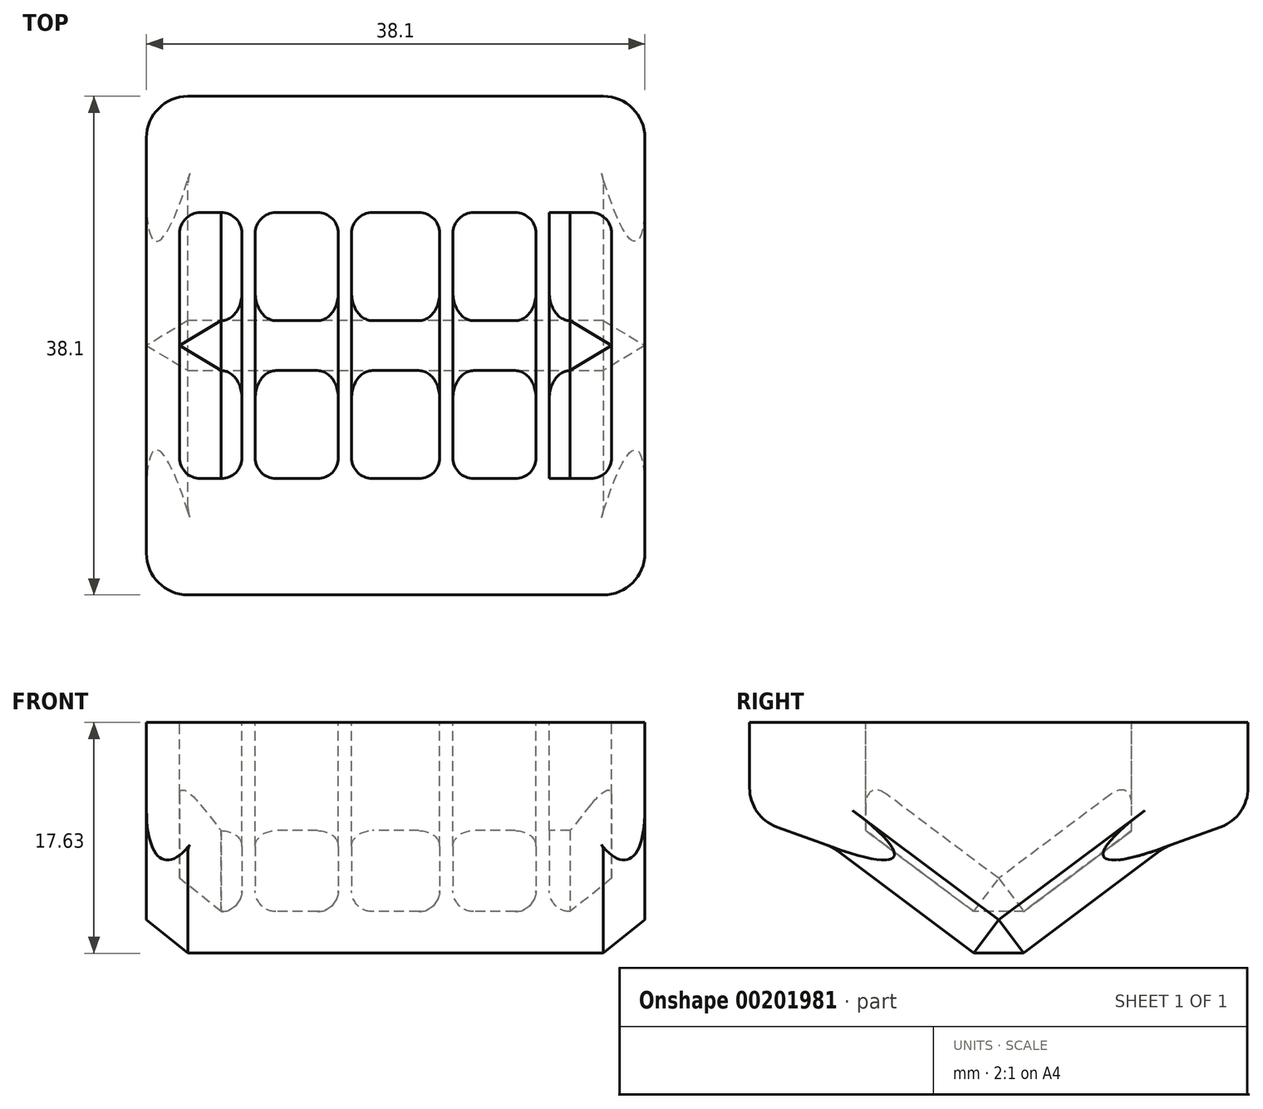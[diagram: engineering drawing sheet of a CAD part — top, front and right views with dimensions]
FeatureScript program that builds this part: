
annotation { "Feature Type Name" : "Feature", "Feature Type Description" : "" }
export const myFeature = defineFeature(function(context is Context, id is Id, definition is map)
    precondition{}
    {
        {
            var Q0;
            Q0=qCreatedBy(makeId("Right.planeOp"),FACE);
            var sketch = newSketch(context, id + "F0", { "sketchPlane" : qUnion([Q0])});
            skLineSegment(sketch, "E0.bottom", {"start": v(12.7, 0) * mm, "end": v(-12.7, 0) * mm});
            skLineSegment(sketch, "E0.top", {"start": v(12.7, 9.53) * mm, "end": v(-12.7, 9.53) * mm});
            skLineSegment(sketch, "E0.left", {"start": v(12.7, 0) * mm, "end": v(12.7, 9.53) * mm});
            skLineSegment(sketch, "E0.right", {"start": v(-12.7, 0) * mm, "end": v(-12.7, 9.53) * mm});
            skPoint(sketch, "E0.middle", {"position": v(0, 4.76) * mm});
            skLineSegment(sketch, "E1", {"start": v(-12.7, 0) * mm, "end": v(0, -9.52) * mm});
            skLineSegment(sketch, "E2", {"start": v(0, -9.52) * mm, "end": v(12.7, 0) * mm});
            skSolve(sketch);
        }
        {
            var Q0;
            Q0 = qSketchRegion(id + "F0", true);
            extrude(context, id + "F1", {"entities" : qUnion([Q0]), "endBound" : BoundingType.SYMMETRIC, "depth" : 38.1 * mm});
        }
        {
            var Q0;
            Q0=makeQuery(id+"F1.opExtrude","SWEPT_FACE",FACE,{"disambiguationData":[OSD([sQuery(id+"F0.wireOp",EDGE,"E0.top")])]});
            shell(context, id + "F2", {"entities" : qUnion([Q0]), "thickness" : 2.54 * mm});
        }
        {
            var Q0;
            Q0=qCreatedBy(makeId("Right.planeOp"),FACE);
            var sketch = newSketch(context, id + "F3", { "sketchPlane" : qUnion([Q0])});
            skLineSegment(sketch, "E3", {"start": v(-12.7, 0) * mm, "end": v(-19.05, 2.31) * mm});
            skLineSegment(sketch, "E4", {"start": v(-19.05, 2.31) * mm, "end": v(-19.05, 9.53) * mm});
            skLineSegment(sketch, "E5", {"start": v(-19.05, 9.53) * mm, "end": v(-12.7, 9.53) * mm});
            skLineSegment(sketch, "E6", {"start": v(-12.7, 9.53) * mm, "end": v(-12.7, 0) * mm});
            skLineSegment(sketch, "E7", {"start": v(0, 0) * mm, "end": v(0, 34.21) * mm, "construction": true});
            skLineSegment(sketch, "E8.MirrorCS", {"start": v(19.05, 2.31) * mm, "end": v(19.05, 9.53) * mm});
            skLineSegment(sketch, "E9.MirrorCS", {"start": v(12.7, 0) * mm, "end": v(19.05, 2.31) * mm});
            skLineSegment(sketch, "E10.MirrorCS", {"start": v(19.05, 9.53) * mm, "end": v(12.7, 9.53) * mm});
            skLineSegment(sketch, "E11.MirrorCS", {"start": v(12.7, 9.53) * mm, "end": v(12.7, 0) * mm});
            skSolve(sketch);
        }
        {
            var Q0;
            Q0 = qSketchRegion(id + "F3", true);
            extrude(context, id + "F4", {"entities" : qUnion([Q0]), "operationType" : NewBodyOperationType.ADD, "endBound" : BoundingType.SYMMETRIC, "depth" : 38.1 * mm});
        }
        {
            var Q0;
            Q0=makeQuery(id+"F4.boolean.opBoolean","MERGE",FACE,{"derivedFrom":[makeQuery(id+"F1.opExtrude","SWEPT_FACE",FACE,{"disambiguationData":[OSD([sQuery(id+"F0.wireOp",EDGE,"E0.top")])]}),makeQuery(id+"F4.opExtrude","SWEPT_FACE",FACE,{"disambiguationData":[OSD([sQuery(id+"F3.wireOp",EDGE,"E5")])]}),makeQuery(id+"F4.opExtrude","SWEPT_FACE",FACE,{"disambiguationData":[OSD([sQuery(id+"F3.wireOp",EDGE,"E10.MirrorCS")])]})]});
            var sketch = newSketch(context, id + "F5", { "sketchPlane" : qUnion([Q0])});
            skLineSegment(sketch, "E12.bottom", {"start": v(-11.75, 10.16) * mm, "end": v(-10.73, 10.16) * mm});
            skLineSegment(sketch, "E12.top", {"start": v(-11.75, -10.16) * mm, "end": v(-10.73, -10.16) * mm});
            skLineSegment(sketch, "E12.left", {"start": v(-11.75, 10.16) * mm, "end": v(-11.75, -10.16) * mm});
            skLineSegment(sketch, "E12.right", {"start": v(-10.73, 10.16) * mm, "end": v(-10.73, -10.16) * mm});
            skPoint(sketch, "E12.middle", {"position": v(-11.24, 0) * mm});
            skLineSegment(sketch, "E13.bottom", {"start": v(-4.38, 10.16) * mm, "end": v(-3.37, 10.16) * mm});
            skLineSegment(sketch, "E13.top", {"start": v(-4.38, -10.16) * mm, "end": v(-3.37, -10.16) * mm});
            skLineSegment(sketch, "E13.left", {"start": v(-4.38, 10.16) * mm, "end": v(-4.38, -10.16) * mm});
            skLineSegment(sketch, "E13.right", {"start": v(-3.37, 10.16) * mm, "end": v(-3.37, -10.16) * mm});
            skPoint(sketch, "E13.middle", {"position": v(-3.87, 0) * mm});
            skLineSegment(sketch, "E14", {"start": v(0, 0) * mm, "end": v(0, 12.03) * mm, "construction": true});
            skPoint(sketch, "E14.endSnap0", {"position": v(0, 10.16) * mm});
            skPoint(sketch, "E15.MirrorP", {"position": v(3.87, 0) * mm});
            skPoint(sketch, "E16.MirrorP", {"position": v(11.24, 0) * mm});
            skLineSegment(sketch, "E17.MirrorCS", {"start": v(4.38, 10.16) * mm, "end": v(4.38, -10.16) * mm});
            skLineSegment(sketch, "E18.MirrorCS", {"start": v(4.38, -10.16) * mm, "end": v(3.37, -10.16) * mm});
            skLineSegment(sketch, "E19.MirrorCS", {"start": v(11.75, -10.16) * mm, "end": v(10.73, -10.16) * mm});
            skLineSegment(sketch, "E20.MirrorCS", {"start": v(10.73, 10.16) * mm, "end": v(10.73, -10.16) * mm});
            skLineSegment(sketch, "E21.MirrorCS", {"start": v(4.38, 10.16) * mm, "end": v(3.37, 10.16) * mm});
            skLineSegment(sketch, "E22.MirrorCS", {"start": v(11.75, 10.16) * mm, "end": v(10.73, 10.16) * mm});
            skLineSegment(sketch, "E23.MirrorCS", {"start": v(3.37, 10.16) * mm, "end": v(3.37, -10.16) * mm});
            skLineSegment(sketch, "E24.MirrorCS", {"start": v(11.75, 10.16) * mm, "end": v(11.75, -10.16) * mm});
            skSolve(sketch);
        }
        {
            var Q0;
            Q0 = qSketchRegion(id + "F5", true);
            extrude(context, id + "F6", {"entities" : qUnion([Q0]), "operationType" : NewBodyOperationType.ADD, "endBound" : BoundingType.UP_TO_NEXT, "oppositeDirection" : true, "depth" : 25.4 * mm});
        }
        {
            var Q0;
            Q0=makeQuery(id+"F1.opExtrude","CAP_EDGE",EDGE,{"disambiguationData":[OSD([sQuery(id+"F0.wireOp",EDGE,"E1")])],"isStart":false});
            var Q1;
            Q1=makeQuery(id+"F1.opExtrude","CAP_EDGE",EDGE,{"disambiguationData":[OSD([sQuery(id+"F0.wireOp",EDGE,"E2")])],"isStart":false});
            var Q2;
            {var subQ0=sQuery(id+"F0.wireOp",EDGE,"E1");Q2=makeQuery(id+"F2.opShell","OFFSET_EDGE",EDGE,{"disambiguationData":[OSD([subQ0]),TDD([makeQuery(id+"F1.opExtrude","CAP_EDGE",EDGE,{"disambiguationData":[OSD([subQ0])],"isStart":false})])]});}
            var Q3;
            {var subQ0=sQuery(id+"F0.wireOp",EDGE,"E2");Q3=makeQuery(id+"F2.opShell","OFFSET_EDGE",EDGE,{"disambiguationData":[OSD([subQ0]),TDD([makeQuery(id+"F1.opExtrude","CAP_EDGE",EDGE,{"disambiguationData":[OSD([subQ0])],"isStart":false})])]});}
            var Q4;
            Q4=makeQuery(id+"F1.opExtrude","CAP_EDGE",EDGE,{"disambiguationData":[OSD([sQuery(id+"F0.wireOp",EDGE,"E1")])],"isStart":true});
            var Q5;
            Q5=makeQuery(id+"F1.opExtrude","CAP_EDGE",EDGE,{"disambiguationData":[OSD([sQuery(id+"F0.wireOp",EDGE,"E2")])],"isStart":true});
            var Q6;
            {var subQ0=sQuery(id+"F0.wireOp",EDGE,"E1");Q6=makeQuery(id+"F2.opShell","OFFSET_EDGE",EDGE,{"disambiguationData":[OSD([subQ0]),TDD([makeQuery(id+"F1.opExtrude","CAP_EDGE",EDGE,{"disambiguationData":[OSD([subQ0])],"isStart":true})])]});}
            var Q7;
            {var subQ0=sQuery(id+"F0.wireOp",EDGE,"E2");Q7=makeQuery(id+"F2.opShell","OFFSET_EDGE",EDGE,{"disambiguationData":[OSD([subQ0]),TDD([makeQuery(id+"F1.opExtrude","CAP_EDGE",EDGE,{"disambiguationData":[OSD([subQ0])],"isStart":true})])]});}
            var Q8;
            Q8=makeQuery(id+"F2.opShell","OFFSET_EDGE",EDGE,{"disambiguationData":[OSD([sQuery(id+"F0.wireOp",EDGE,"E1"),sQuery(id+"F0.wireOp",EDGE,"E2")])]});
            var Q9;
            Q9=makeQuery(id+"F1.opExtrude","SWEPT_EDGE",EDGE,{"disambiguationData":[OSD([sQuery(id+"F0.wireOp",EDGE,"E1"),sQuery(id+"F0.wireOp",EDGE,"E2")])]});
            chamfer(context, id + "F7", {"entities" : qUnion([Q0, Q1, Q2, Q3, Q4, Q5, Q6, Q7, Q8, Q9]), "width" : 3.17 * mm, "tangentPropagation" : true});
        }
        {
            var Q0;
            Q0=makeQuery(id+"F4.opExtrude","CAP_EDGE",EDGE,{"disambiguationData":[OSD([sQuery(id+"F3.wireOp",EDGE,"E3")])],"isStart":true});
            var Q1;
            Q1=makeQuery(id+"F4.opExtrude","CAP_EDGE",EDGE,{"disambiguationData":[OSD([sQuery(id+"F3.wireOp",EDGE,"E9.MirrorCS")])],"isStart":true});
            var Q2;
            Q2=makeQuery(id+"F4.opExtrude","CAP_EDGE",EDGE,{"disambiguationData":[OSD([sQuery(id+"F3.wireOp",EDGE,"E8.MirrorCS")])],"isStart":true});
            var Q3;
            Q3=makeQuery(id+"F4.opExtrude","CAP_EDGE",EDGE,{"disambiguationData":[OSD([sQuery(id+"F3.wireOp",EDGE,"E4")])],"isStart":true});
            var Q4;
            Q4=makeQuery(id+"F4.opExtrude","CAP_EDGE",EDGE,{"disambiguationData":[OSD([sQuery(id+"F3.wireOp",EDGE,"E3")])],"isStart":false});
            var Q5;
            Q5=makeQuery(id+"F4.opExtrude","CAP_EDGE",EDGE,{"disambiguationData":[OSD([sQuery(id+"F3.wireOp",EDGE,"E9.MirrorCS")])],"isStart":false});
            var Q6;
            Q6=makeQuery(id+"F4.opExtrude","CAP_EDGE",EDGE,{"disambiguationData":[OSD([sQuery(id+"F3.wireOp",EDGE,"E4")])],"isStart":false});
            var Q7;
            Q7=makeQuery(id+"F4.boolean.opBoolean","MERGE",EDGE,{"derivedFrom":[makeQuery(id+"F1.opExtrude","SWEPT_EDGE",EDGE,{"disambiguationData":[OSD([sQuery(id+"F0.wireOp",EDGE,"E0.bottom"),sQuery(id+"F0.wireOp",EDGE,"E0.right"),sQuery(id+"F0.wireOp",EDGE,"E1")])]}),makeQuery(id+"F4.opExtrude","SWEPT_EDGE",EDGE,{"disambiguationData":[OSD([sQuery(id+"F3.wireOp",EDGE,"E3"),sQuery(id+"F3.wireOp",EDGE,"E6")])]})]});
            var Q8;
            Q8=makeQuery(id+"F4.opExtrude","SWEPT_EDGE",EDGE,{"disambiguationData":[OSD([sQuery(id+"F3.wireOp",EDGE,"E3"),sQuery(id+"F3.wireOp",EDGE,"E4")])]});
            var Q9;
            Q9=makeQuery(id+"F4.boolean.opBoolean","MERGE",EDGE,{"derivedFrom":[makeQuery(id+"F1.opExtrude","SWEPT_EDGE",EDGE,{"disambiguationData":[OSD([sQuery(id+"F0.wireOp",EDGE,"E0.bottom"),sQuery(id+"F0.wireOp",EDGE,"E0.left"),sQuery(id+"F0.wireOp",EDGE,"E2")])]}),makeQuery(id+"F4.opExtrude","SWEPT_EDGE",EDGE,{"disambiguationData":[OSD([sQuery(id+"F3.wireOp",EDGE,"E9.MirrorCS"),sQuery(id+"F3.wireOp",EDGE,"E11.MirrorCS")])]})]});
            var Q10;
            Q10=makeQuery(id+"F4.opExtrude","SWEPT_EDGE",EDGE,{"disambiguationData":[OSD([sQuery(id+"F3.wireOp",EDGE,"E8.MirrorCS"),sQuery(id+"F3.wireOp",EDGE,"E9.MirrorCS")])]});
            var Q11;
            Q11=makeQuery(id+"F4.opExtrude","CAP_EDGE",EDGE,{"disambiguationData":[OSD([sQuery(id+"F3.wireOp",EDGE,"E8.MirrorCS")])],"isStart":false});
            fillet(context, id + "F8", {"entities" : qUnion([Q0, Q1, Q2, Q3, Q4, Q5, Q6, Q7, Q8, Q9, Q10, Q11]), "radius" : 3.17 * mm, "tangentPropagation" : true, "allowEdgeOverflow" : false});
        }
        {
            var Q0;
            {var subQ0=sQuery(id+"F0.wireOp",EDGE,"E0.right");Q0=makeQuery(id+"F2.opShell","OFFSET_EDGE",EDGE,{"disambiguationData":[OSD([subQ0]),TDD([makeQuery(id+"F1.opExtrude","CAP_EDGE",EDGE,{"disambiguationData":[OSD([subQ0])],"isStart":false})])]});}
            var Q1;
            Q1=makeQuery(id+"F6.opExtrude","SWEPT_EDGE",EDGE,{"disambiguationData":[OSD([sQuery(id+"F0.wireOp",EDGE,"E0.top"),sQuery(id+"F0.wireOp",EDGE,"E0.right"),sQuery(id+"F5.wireOp",EDGE,"E19.MirrorCS"),sQuery(id+"F5.wireOp",EDGE,"E20.MirrorCS")])]});
            var Q2;
            Q2=makeQuery(id+"F6.opExtrude","SWEPT_EDGE",EDGE,{"disambiguationData":[OSD([sQuery(id+"F0.wireOp",EDGE,"E0.top"),sQuery(id+"F0.wireOp",EDGE,"E0.right"),sQuery(id+"F5.wireOp",EDGE,"E18.MirrorCS"),sQuery(id+"F5.wireOp",EDGE,"E23.MirrorCS")])]});
            var Q3;
            Q3=makeQuery(id+"F6.opExtrude","SWEPT_EDGE",EDGE,{"disambiguationData":[OSD([sQuery(id+"F0.wireOp",EDGE,"E0.top"),sQuery(id+"F0.wireOp",EDGE,"E0.right"),sQuery(id+"F5.wireOp",EDGE,"E13.top"),sQuery(id+"F5.wireOp",EDGE,"E13.left")])]});
            var Q4;
            Q4=makeQuery(id+"F6.opExtrude","SWEPT_EDGE",EDGE,{"disambiguationData":[OSD([sQuery(id+"F0.wireOp",EDGE,"E0.top"),sQuery(id+"F0.wireOp",EDGE,"E0.right"),sQuery(id+"F5.wireOp",EDGE,"E12.top"),sQuery(id+"F5.wireOp",EDGE,"E12.left")])]});
            var Q5;
            Q5=makeQuery(id+"F6.opExtrude","SWEPT_EDGE",EDGE,{"disambiguationData":[OSD([sQuery(id+"F0.wireOp",EDGE,"E0.top"),sQuery(id+"F0.wireOp",EDGE,"E0.right"),sQuery(id+"F5.wireOp",EDGE,"E19.MirrorCS"),sQuery(id+"F5.wireOp",EDGE,"E24.MirrorCS")])]});
            var Q6;
            Q6=makeQuery(id+"F6.opExtrude","SWEPT_EDGE",EDGE,{"disambiguationData":[OSD([sQuery(id+"F0.wireOp",EDGE,"E0.top"),sQuery(id+"F0.wireOp",EDGE,"E0.right"),sQuery(id+"F5.wireOp",EDGE,"E17.MirrorCS"),sQuery(id+"F5.wireOp",EDGE,"E18.MirrorCS")])]});
            var Q7;
            Q7=makeQuery(id+"F6.opExtrude","SWEPT_EDGE",EDGE,{"disambiguationData":[OSD([sQuery(id+"F0.wireOp",EDGE,"E0.top"),sQuery(id+"F0.wireOp",EDGE,"E0.right"),sQuery(id+"F5.wireOp",EDGE,"E13.top"),sQuery(id+"F5.wireOp",EDGE,"E13.right")])]});
            var Q8;
            Q8=makeQuery(id+"F6.opExtrude","SWEPT_EDGE",EDGE,{"disambiguationData":[OSD([sQuery(id+"F0.wireOp",EDGE,"E0.top"),sQuery(id+"F0.wireOp",EDGE,"E0.right"),sQuery(id+"F5.wireOp",EDGE,"E12.top"),sQuery(id+"F5.wireOp",EDGE,"E12.right")])]});
            var Q9;
            {var subQ0=sQuery(id+"F0.wireOp",EDGE,"E0.right");Q9=makeQuery(id+"F2.opShell","OFFSET_EDGE",EDGE,{"disambiguationData":[OSD([subQ0]),TDD([makeQuery(id+"F1.opExtrude","CAP_EDGE",EDGE,{"disambiguationData":[OSD([subQ0])],"isStart":true})])]});}
            var Q10;
            Q10=makeQuery(id+"F6.opExtrude","SWEPT_EDGE",EDGE,{"disambiguationData":[OSD([sQuery(id+"F0.wireOp",EDGE,"E0.top"),sQuery(id+"F0.wireOp",EDGE,"E0.left"),sQuery(id+"F5.wireOp",EDGE,"E22.MirrorCS"),sQuery(id+"F5.wireOp",EDGE,"E24.MirrorCS")])]});
            var Q11;
            Q11=makeQuery(id+"F6.opExtrude","SWEPT_EDGE",EDGE,{"disambiguationData":[OSD([sQuery(id+"F0.wireOp",EDGE,"E0.top"),sQuery(id+"F0.wireOp",EDGE,"E0.left"),sQuery(id+"F5.wireOp",EDGE,"E17.MirrorCS"),sQuery(id+"F5.wireOp",EDGE,"E21.MirrorCS")])]});
            var Q12;
            Q12=makeQuery(id+"F6.opExtrude","SWEPT_EDGE",EDGE,{"disambiguationData":[OSD([sQuery(id+"F0.wireOp",EDGE,"E0.top"),sQuery(id+"F0.wireOp",EDGE,"E0.left"),sQuery(id+"F5.wireOp",EDGE,"E13.bottom"),sQuery(id+"F5.wireOp",EDGE,"E13.right")])]});
            var Q13;
            Q13=makeQuery(id+"F6.opExtrude","SWEPT_EDGE",EDGE,{"disambiguationData":[OSD([sQuery(id+"F0.wireOp",EDGE,"E0.top"),sQuery(id+"F0.wireOp",EDGE,"E0.left"),sQuery(id+"F5.wireOp",EDGE,"E12.bottom"),sQuery(id+"F5.wireOp",EDGE,"E12.right")])]});
            var Q14;
            {var subQ0=sQuery(id+"F0.wireOp",EDGE,"E0.left");Q14=makeQuery(id+"F2.opShell","OFFSET_EDGE",EDGE,{"disambiguationData":[OSD([subQ0]),TDD([makeQuery(id+"F1.opExtrude","CAP_EDGE",EDGE,{"disambiguationData":[OSD([subQ0])],"isStart":true})])]});}
            var Q15;
            {var subQ0=sQuery(id+"F0.wireOp",EDGE,"E0.left");Q15=makeQuery(id+"F2.opShell","OFFSET_EDGE",EDGE,{"disambiguationData":[OSD([subQ0]),TDD([makeQuery(id+"F1.opExtrude","CAP_EDGE",EDGE,{"disambiguationData":[OSD([subQ0])],"isStart":false})])]});}
            var Q16;
            Q16=makeQuery(id+"F6.opExtrude","SWEPT_EDGE",EDGE,{"disambiguationData":[OSD([sQuery(id+"F0.wireOp",EDGE,"E0.top"),sQuery(id+"F0.wireOp",EDGE,"E0.left"),sQuery(id+"F5.wireOp",EDGE,"E20.MirrorCS"),sQuery(id+"F5.wireOp",EDGE,"E22.MirrorCS")])]});
            var Q17;
            Q17=makeQuery(id+"F6.opExtrude","SWEPT_EDGE",EDGE,{"disambiguationData":[OSD([sQuery(id+"F0.wireOp",EDGE,"E0.top"),sQuery(id+"F0.wireOp",EDGE,"E0.left"),sQuery(id+"F5.wireOp",EDGE,"E21.MirrorCS"),sQuery(id+"F5.wireOp",EDGE,"E23.MirrorCS")])]});
            var Q18;
            Q18=makeQuery(id+"F6.opExtrude","SWEPT_EDGE",EDGE,{"disambiguationData":[OSD([sQuery(id+"F0.wireOp",EDGE,"E0.top"),sQuery(id+"F0.wireOp",EDGE,"E0.left"),sQuery(id+"F5.wireOp",EDGE,"E13.bottom"),sQuery(id+"F5.wireOp",EDGE,"E13.left")])]});
            var Q19;
            Q19=makeQuery(id+"F6.opExtrude","SWEPT_EDGE",EDGE,{"disambiguationData":[OSD([sQuery(id+"F0.wireOp",EDGE,"E0.top"),sQuery(id+"F0.wireOp",EDGE,"E0.left"),sQuery(id+"F5.wireOp",EDGE,"E12.bottom"),sQuery(id+"F5.wireOp",EDGE,"E12.left")])]});
            var Q20;
            {var subQ0=makeQuery(id+"F6.opExtrude","SWEPT_FACE",FACE,{"disambiguationData":[OSD([sQuery(id+"F5.wireOp",EDGE,"E13.right")])]});var subQ1=sQuery(id+"F0.wireOp",EDGE,"E1");var subQ2=sQuery(id+"F0.wireOp",EDGE,"E2");Q20=makeQuery(id+"F7.opChamfer","BLEND_EDGE",EDGE,{"blendedFrom":[makeQuery(id+"F6.boolean.opBoolean","SPLIT",EDGE,{"disambiguationData":[TD([subQ0])],"derivedFrom":makeQuery(id+"F2.opShell","OFFSET_EDGE",EDGE,{"disambiguationData":[OSD([subQ1,subQ2])]})}),subQ0],"blendedInto":[subQ0]});}
            var Q21;
            {var subQ0=makeQuery(id+"F6.opExtrude","SWEPT_FACE",FACE,{"disambiguationData":[OSD([sQuery(id+"F5.wireOp",EDGE,"E24.MirrorCS")])]});var subQ1=sQuery(id+"F0.wireOp",EDGE,"E2");var subQ2=sQuery(id+"F0.wireOp",EDGE,"E1");Q21=makeQuery(id+"F7.opChamfer","BLEND_EDGE",EDGE,{"blendedFrom":[makeQuery(id+"F6.boolean.opBoolean","SPLIT",EDGE,{"disambiguationData":[TD([subQ0])],"derivedFrom":makeQuery(id+"F2.opShell","OFFSET_EDGE",EDGE,{"disambiguationData":[OSD([subQ2,subQ1])]})}),subQ0],"blendedInto":[subQ0]});}
            var Q22;
            {var subQ0=makeQuery(id+"F6.opExtrude","SWEPT_FACE",FACE,{"disambiguationData":[OSD([sQuery(id+"F5.wireOp",EDGE,"E17.MirrorCS")])]});var subQ1=sQuery(id+"F0.wireOp",EDGE,"E1");var subQ2=sQuery(id+"F0.wireOp",EDGE,"E2");Q22=makeQuery(id+"F7.opChamfer","BLEND_EDGE",EDGE,{"blendedFrom":[makeQuery(id+"F6.boolean.opBoolean","SPLIT",EDGE,{"disambiguationData":[TD([subQ0])],"derivedFrom":makeQuery(id+"F2.opShell","OFFSET_EDGE",EDGE,{"disambiguationData":[OSD([subQ1,subQ2])]})}),subQ0],"blendedInto":[subQ0]});}
            var Q23;
            {var subQ0=makeQuery(id+"F6.opExtrude","SWEPT_FACE",FACE,{"disambiguationData":[OSD([sQuery(id+"F5.wireOp",EDGE,"E12.right")])]});var subQ1=sQuery(id+"F0.wireOp",EDGE,"E1");var subQ2=sQuery(id+"F0.wireOp",EDGE,"E2");Q23=makeQuery(id+"F7.opChamfer","BLEND_EDGE",EDGE,{"blendedFrom":[makeQuery(id+"F6.boolean.opBoolean","SPLIT",EDGE,{"disambiguationData":[TD([subQ0])],"derivedFrom":makeQuery(id+"F2.opShell","OFFSET_EDGE",EDGE,{"disambiguationData":[OSD([subQ1,subQ2])]})}),subQ0],"blendedInto":[subQ0]});}
            var Q24;
            {var subQ0=makeQuery(id+"F6.opExtrude","SWEPT_FACE",FACE,{"disambiguationData":[OSD([sQuery(id+"F5.wireOp",EDGE,"E20.MirrorCS")])]});var subQ1=sQuery(id+"F0.wireOp",EDGE,"E1");var subQ2=sQuery(id+"F0.wireOp",EDGE,"E2");Q24=makeQuery(id+"F7.opChamfer","BLEND_EDGE",EDGE,{"blendedFrom":[makeQuery(id+"F6.boolean.opBoolean","SPLIT",EDGE,{"disambiguationData":[TD([makeQuery(id+"F6.opExtrude","SWEPT_FACE",FACE,{"disambiguationData":[OSD([sQuery(id+"F5.wireOp",EDGE,"E17.MirrorCS")])]})])],"derivedFrom":makeQuery(id+"F2.opShell","OFFSET_EDGE",EDGE,{"disambiguationData":[OSD([subQ1,subQ2])]})}),subQ0],"blendedInto":[subQ0]});}
            var Q25;
            {var subQ0=makeQuery(id+"F6.opExtrude","SWEPT_FACE",FACE,{"disambiguationData":[OSD([sQuery(id+"F5.wireOp",EDGE,"E23.MirrorCS")])]});var subQ1=sQuery(id+"F0.wireOp",EDGE,"E1");var subQ2=sQuery(id+"F0.wireOp",EDGE,"E2");Q25=makeQuery(id+"F7.opChamfer","BLEND_EDGE",EDGE,{"blendedFrom":[makeQuery(id+"F6.boolean.opBoolean","SPLIT",EDGE,{"disambiguationData":[TD([makeQuery(id+"F6.opExtrude","SWEPT_FACE",FACE,{"disambiguationData":[OSD([sQuery(id+"F5.wireOp",EDGE,"E13.right")])]})])],"derivedFrom":makeQuery(id+"F2.opShell","OFFSET_EDGE",EDGE,{"disambiguationData":[OSD([subQ1,subQ2])]})}),subQ0],"blendedInto":[subQ0]});}
            var Q26;
            {var subQ0=makeQuery(id+"F6.opExtrude","SWEPT_FACE",FACE,{"disambiguationData":[OSD([sQuery(id+"F5.wireOp",EDGE,"E13.left")])]});var subQ1=sQuery(id+"F0.wireOp",EDGE,"E1");var subQ2=sQuery(id+"F0.wireOp",EDGE,"E2");Q26=makeQuery(id+"F7.opChamfer","BLEND_EDGE",EDGE,{"blendedFrom":[makeQuery(id+"F6.boolean.opBoolean","SPLIT",EDGE,{"disambiguationData":[TD([makeQuery(id+"F6.opExtrude","SWEPT_FACE",FACE,{"disambiguationData":[OSD([sQuery(id+"F5.wireOp",EDGE,"E12.right")])]})])],"derivedFrom":makeQuery(id+"F2.opShell","OFFSET_EDGE",EDGE,{"disambiguationData":[OSD([subQ1,subQ2])]})}),subQ0],"blendedInto":[subQ0]});}
            var Q27;
            {var subQ0=makeQuery(id+"F6.opExtrude","SWEPT_FACE",FACE,{"disambiguationData":[OSD([sQuery(id+"F5.wireOp",EDGE,"E12.left")])]});var subQ1=sQuery(id+"F0.wireOp",EDGE,"E2");var subQ2=sQuery(id+"F0.wireOp",EDGE,"E1");Q27=makeQuery(id+"F7.opChamfer","BLEND_EDGE",EDGE,{"blendedFrom":[makeQuery(id+"F6.boolean.opBoolean","SPLIT",EDGE,{"disambiguationData":[TD([subQ0])],"derivedFrom":makeQuery(id+"F2.opShell","OFFSET_EDGE",EDGE,{"disambiguationData":[OSD([subQ2,subQ1])]})}),subQ0],"blendedInto":[subQ0]});}
            fillet(context, id + "F9", {"entities" : qUnion([Q0, Q1, Q2, Q3, Q4, Q5, Q6, Q7, Q8, Q9, Q10, Q11, Q12, Q13, Q14, Q15, Q16, Q17, Q18, Q19, Q20, Q21, Q22, Q23, Q24, Q25, Q26, Q27]), "radius" : 1.59 * mm, "tangentPropagation" : true, "allowEdgeOverflow" : false});
        }
    });
